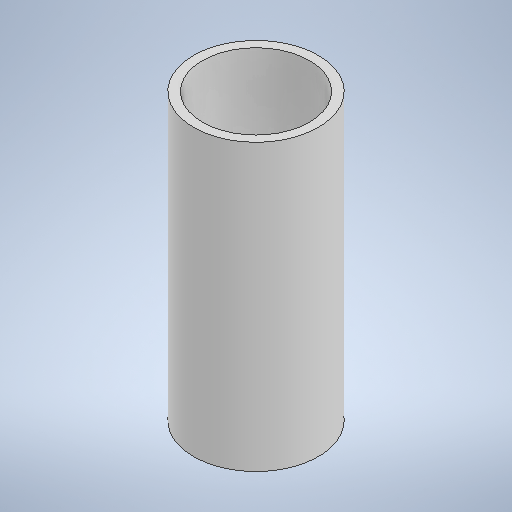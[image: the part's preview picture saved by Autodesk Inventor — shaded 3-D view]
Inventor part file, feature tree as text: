
AUTODESK INVENTOR PART (.ipt)
format: ipt  version: 2025 (Build 290162010, 162A)  size: 221,184 bytes
history: native  units: mm
features: extrude x1, sketch x1
ambient origin geometry x8: Origin, YZ Plane, XZ Plane, XY Plane, X Axis, Y Axis, Z Axis, Center Point
bodies: Solid1 (feature_tree)
feature tree (2):
  extrude  "Extrusion1"  Depth=203.2mm
  sketch  "Sketch1"  dims[d0=88.9mm d1=76.2mm d2=203.2mm d3=0.0mm]
